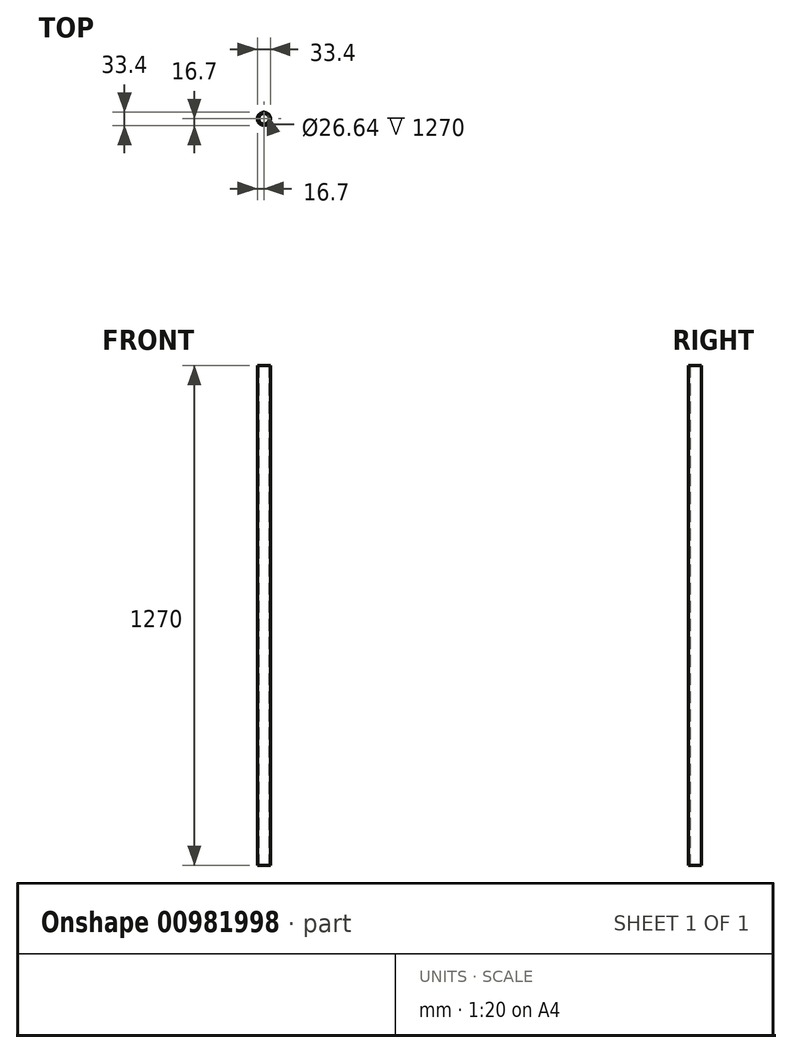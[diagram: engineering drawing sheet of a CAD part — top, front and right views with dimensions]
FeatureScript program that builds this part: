
annotation { "Feature Type Name" : "Feature", "Feature Type Description" : "" }
export const myFeature = defineFeature(function(context is Context, id is Id, definition is map)
    precondition{}
    {
        {
            var Q0;
            Q0=qCreatedBy(makeId("Top.planeOp"),FACE);
            var sketch = newSketch(context, id + "F0", { "sketchPlane" : qUnion([Q0])});
            skCircle(sketch, "E0", {"center": v(0, 0) * mm, "radius": 13.32 * mm});
            skCircle(sketch, "E1", {"center": v(0, 0) * mm, "radius": 16.7 * mm});
            skSolve(sketch);
        }
        {
            var Q0;
            Q0 = qSketchRegion(id + "F0", true);
            extrude(context, id + "F1", {"entities" : qUnion([Q0]), "depth" : 1270 * mm, "offsetDistance" : 25.4 * mm});
        }
    });
